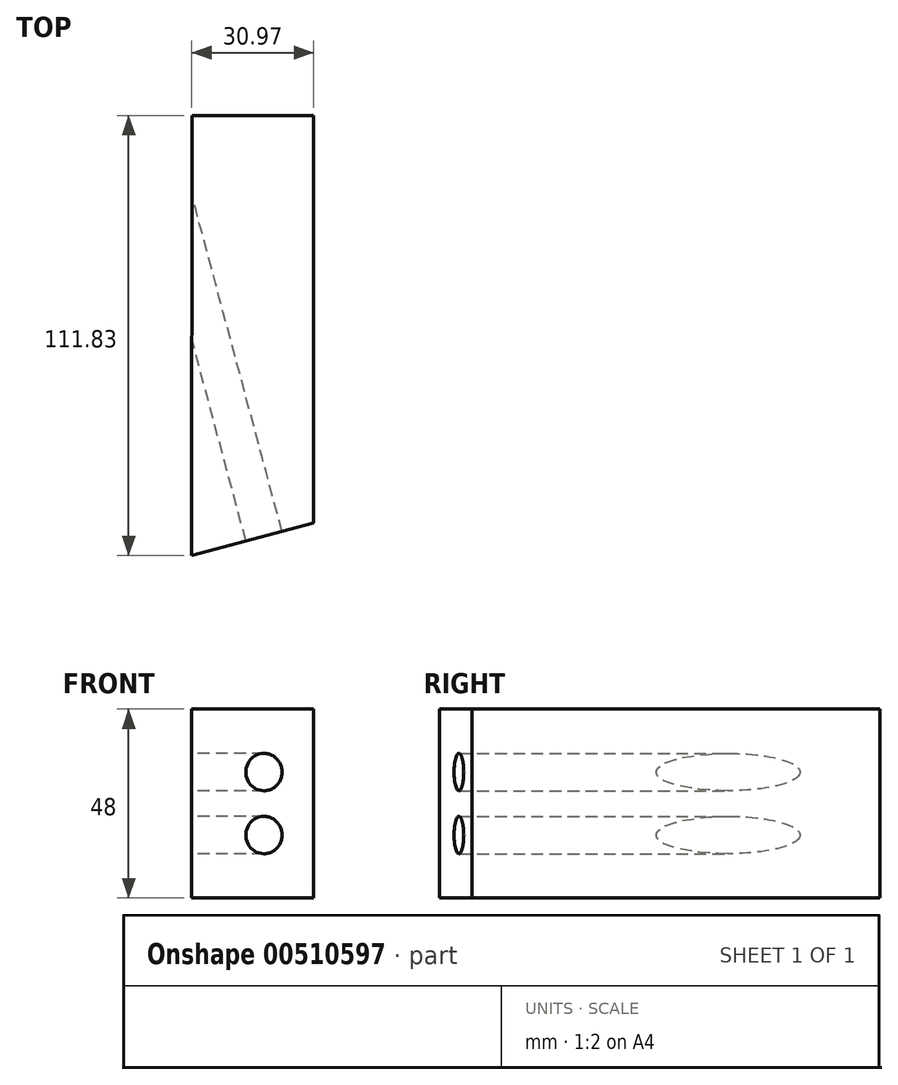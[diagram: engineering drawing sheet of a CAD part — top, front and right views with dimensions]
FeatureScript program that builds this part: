
annotation { "Feature Type Name" : "Feature", "Feature Type Description" : "" }
export const myFeature = defineFeature(function(context is Context, id is Id, definition is map)
    precondition{}
    {
        {
            var Q0;
            Q0=qCreatedBy(makeId("Front.planeOp"),FACE);
            var sketch = newSketch(context, id + "F0", { "sketchPlane" : qUnion([Q0])});
            skLineSegment(sketch, "E0.bottom", {"start": v(-18.29, 29.8) * mm, "end": v(41.71, 29.8) * mm});
            skLineSegment(sketch, "E0.top", {"start": v(-18.29, -18.2) * mm, "end": v(41.71, -18.2) * mm});
            skLineSegment(sketch, "E0.left", {"start": v(-18.29, 29.8) * mm, "end": v(-18.29, -18.2) * mm});
            skLineSegment(sketch, "E0.right", {"start": v(41.71, 29.8) * mm, "end": v(41.71, -18.2) * mm});
            skCircle(sketch, "E1", {"center": v(0.71, -2.2) * mm, "radius": 4.75 * mm});
            skCircle(sketch, "E2", {"center": v(0.71, 13.8) * mm, "radius": 4.75 * mm});
            skSolve(sketch);
        }
        {
            var Q0;
            Q0=makeQuery(id+"F0.imprint","IMPRINT",FACE,{"disambiguationData":[TD([[makeQuery(id+"F0.imprint","IMPRINT",EDGE,{"derivedFrom":sQuery(id+"F0.wireOp",EDGE,"E0.bottom")}),-1.0]])]});
            extrude(context, id + "F1", {"entities" : qUnion([Q0]), "depth" : 108 * mm});
        }
        {
            var Q0;
            Q0=makeQuery(id+"F1.opExtrude","SWEPT_FACE",FACE,{"disambiguationData":[OSD([sQuery(id+"F0.wireOp",EDGE,"E0.top")])]});
            var sketch = newSketch(context, id + "F2", { "sketchPlane" : qUnion([Q0])});
            skLineSegment(sketch, "E3", {"start": v(-18.29, 108) * mm, "end": v(10.71, 0) * mm});
            skLineSegment(sketch, "E4", {"start": v(10.71, 0) * mm, "end": v(-18.29, 0) * mm});
            skLineSegment(sketch, "E5", {"start": v(-18.29, 0) * mm, "end": v(-18.29, 108) * mm});
            skSolve(sketch);
        }
        {
            var Q0;
            Q0 = qSketchRegion(id + "F2", true);
            extrude(context, id + "F3", {"entities" : qUnion([Q0]), "operationType" : NewBodyOperationType.REMOVE, "oppositeDirection" : true, "depth" : 48 * mm});
        }
        {
            var Q0;
            Q0=makeQuery(id+"F1.opExtrude","SWEPT_FACE",FACE,{"disambiguationData":[OSD([sQuery(id+"F0.wireOp",EDGE,"E0.top")])]});
            var sketch = newSketch(context, id + "F4", { "sketchPlane" : qUnion([Q0])});
            skLineSegment(sketch, "E6", {"start": v(13.71, 108) * mm, "end": v(42.3, 1.5) * mm});
            skLineSegment(sketch, "E7", {"start": v(42.3, 1.5) * mm, "end": v(42.3, 108) * mm});
            skLineSegment(sketch, "E8", {"start": v(42.3, 108) * mm, "end": v(13.71, 108) * mm});
            skSolve(sketch);
        }
        {
            var Q0;
            {var subQ0=sQuery(id+"F4.wireOp",EDGE,"E7");Q0=makeQuery(id+"F4.imprint","IMPRINT",FACE,{"disambiguationData":[TD([[makeQuery(id+"F4.imprint","IMPRINT",EDGE,{"derivedFrom":subQ0}),1.0]])]});}
            var Q1;
            {var subQ0=sQuery(id+"F4.wireOp",EDGE,"E8");var subQ1=sQuery(id+"F4.wireOp",EDGE,"E6");var subQ2=sQuery(id+"F0.wireOp",EDGE,"E0.top");var subQ3=makeQuery(id+"F4.imprint","INTERSECT",VERTEX,{"derivedFrom":[makeQuery(id+"F1.opExtrude","CAP_EDGE",EDGE,{"disambiguationData":[OSD([subQ2])],"isStart":false}),subQ1,subQ0]});Q1=makeQuery(id+"F4.imprint","IMPRINT",FACE,{"disambiguationData":[TD([[makeQuery(id+"F4.imprint","IMPRINT",EDGE,{"disambiguationData":[TD([[subQ3,-1.0]])],"derivedFrom":subQ1}),1.0]])]});}
            extrude(context, id + "F5", {"entities" : qUnion([Q0, Q1]), "operationType" : NewBodyOperationType.REMOVE, "oppositeDirection" : true, "depth" : 48 * mm});
        }
        {
            var Q0;
            Q0=makeQuery(id+"F1.opExtrude","SWEPT_FACE",FACE,{"disambiguationData":[OSD([sQuery(id+"F0.wireOp",EDGE,"E0.top")])]});
            var sketch = newSketch(context, id + "F6", { "sketchPlane" : qUnion([Q0])});
            skLineSegment(sketch, "E9", {"start": v(10.71, 0) * mm, "end": v(41.71, 3.72) * mm});
            skLineSegment(sketch, "E10", {"start": v(41.71, 3.72) * mm, "end": v(41.71, 0) * mm});
            skLineSegment(sketch, "E11", {"start": v(41.71, 0) * mm, "end": v(10.71, 0) * mm});
            skSolve(sketch);
        }
        {
            var Q0;
            Q0=makeQuery(id+"F6.imprint","IMPRINT",FACE,{"disambiguationData":[TD([[makeQuery(id+"F6.imprint","IMPRINT",EDGE,{"derivedFrom":sQuery(id+"F6.wireOp",EDGE,"E9")}),-1.0]])]});
            extrude(context, id + "F7", {"entities" : qUnion([Q0]), "operationType" : NewBodyOperationType.REMOVE, "oppositeDirection" : true, "depth" : 48 * mm});
        }
        {
            var Q0;
            Q0=makeQuery(id+"F1.opExtrude","SWEPT_FACE",FACE,{"disambiguationData":[OSD([sQuery(id+"F0.wireOp",EDGE,"E0.top")])]});
            var sketch = newSketch(context, id + "F8", { "sketchPlane" : qUnion([Q0])});
            skLineSegment(sketch, "E12", {"start": v(10.71, 0) * mm, "end": v(40.56, 8.01) * mm});
            skLineSegment(sketch, "E13", {"start": v(40.56, 8.01) * mm, "end": v(42.38, 1.24) * mm});
            skLineSegment(sketch, "E14", {"start": v(42.38, 1.24) * mm, "end": v(10.71, 0) * mm});
            skSolve(sketch);
        }
        {
            var Q0;
            Q0 = qSketchRegion(id + "F8", true);
            extrude(context, id + "F9", {"entities" : qUnion([Q0]), "operationType" : NewBodyOperationType.REMOVE, "oppositeDirection" : true, "depth" : 48 * mm});
        }
        {
            var Q0;
            Q0=makeQuery(id+"F1.opExtrude","SWEPT_BODY",BODY,{"disambiguationData":[OSD([sQuery(id+"F0.wireOp",EDGE,"E0.bottom"),sQuery(id+"F0.wireOp",EDGE,"E0.top"),sQuery(id+"F0.wireOp",EDGE,"E0.left"),sQuery(id+"F0.wireOp",EDGE,"E0.right"),sQuery(id+"F0.wireOp",EDGE,"E1"),sQuery(id+"F0.wireOp",EDGE,"E2")])]});
            var Q1;
            Q1=makeQuery(id+"F3.boolean.opBoolean","MERGE",EDGE,{"derivedFrom":[makeQuery(id+"F1.opExtrude","CAP_EDGE",EDGE,{"disambiguationData":[OSD([sQuery(id+"F0.wireOp",EDGE,"E0.left")])],"isStart":false}),makeQuery(id+"F3.opExtrude","SWEPT_EDGE",EDGE,{"disambiguationData":[OSD([sQuery(id+"F0.wireOp",EDGE,"E0.top"),sQuery(id+"F2.wireOp",EDGE,"E3"),sQuery(id+"F2.wireOp",EDGE,"E5")])]})]});
            transform(context, id + "F10", {"entities" : qUnion([Q0]), "transformType" : TransformType.ROTATION, "transformAxis" : qUnion([Q1]), "angle" : 15 * degree, "oppositeDirection" : true, "makeCopy" : false});
        }
    });
